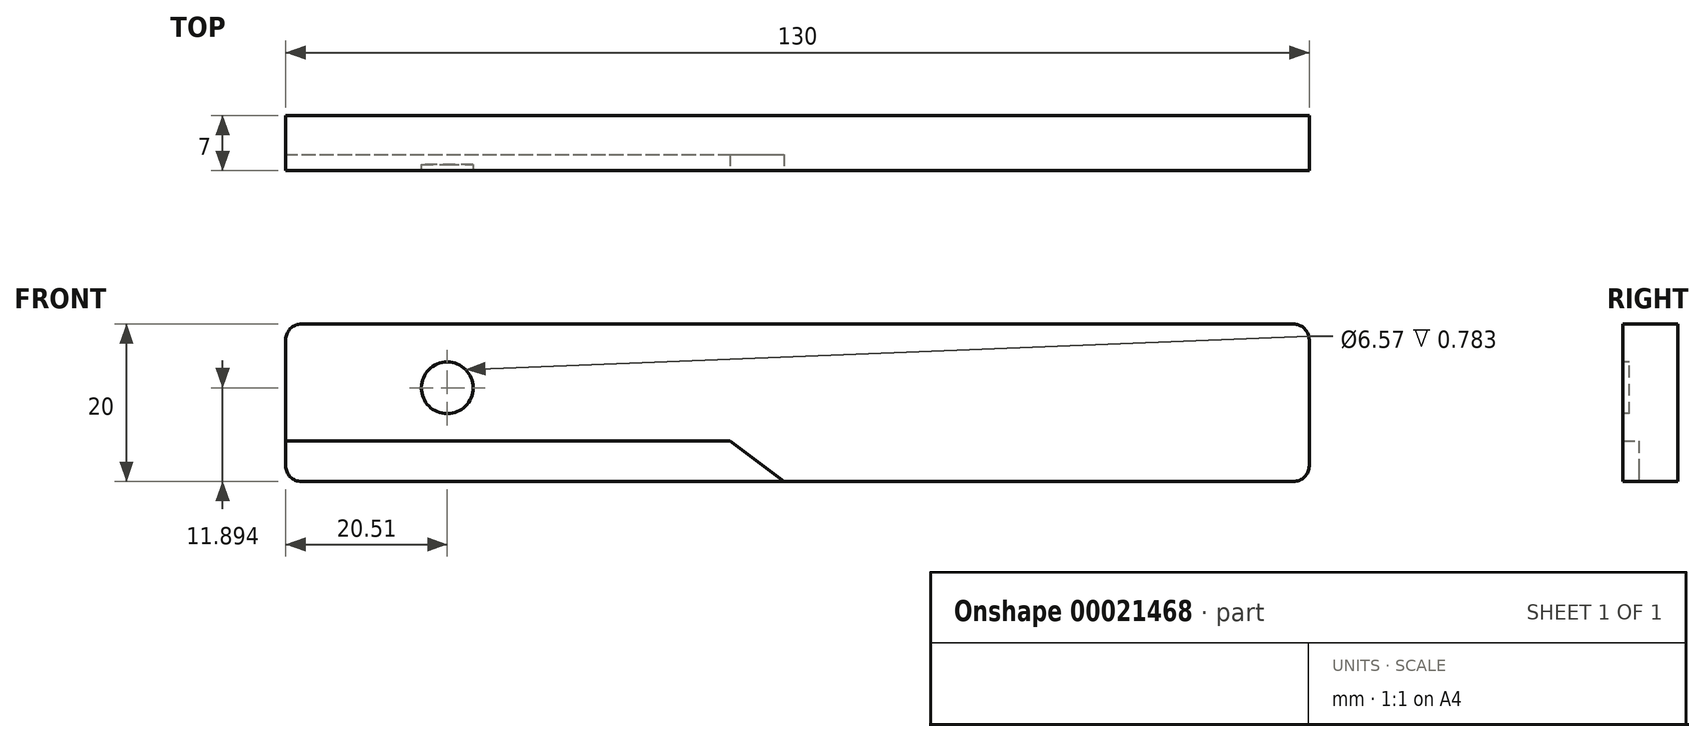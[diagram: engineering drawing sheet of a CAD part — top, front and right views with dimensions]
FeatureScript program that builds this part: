
annotation { "Feature Type Name" : "Feature", "Feature Type Description" : "" }
export const myFeature = defineFeature(function(context is Context, id is Id, definition is map)
    precondition{}
    {
        {
            var Q0;
            Q0=qCreatedBy(makeId("Front.planeOp"),FACE);
            var sketch = newSketch(context, id + "F0", { "sketchPlane" : qUnion([Q0])});
            skLineSegment(sketch, "E0.rect.bottom", {"start": v(63, -10) * mm, "end": v(-63, -10) * mm});
            skLineSegment(sketch, "E0.rect.top", {"start": v(63, 10) * mm, "end": v(-63, 10) * mm});
            skLineSegment(sketch, "E0.rect.left", {"start": v(65, -8) * mm, "end": v(65, 8) * mm});
            skLineSegment(sketch, "E0.rect.right", {"start": v(-65, -8) * mm, "end": v(-65, 8) * mm});
            skPoint(sketch, "E0.rect.middle", {"position": v(0, 0) * mm});
            skPoint(sketch, "E1.visualSharp", {"position": v(-65, 10) * mm});
            skArc(sketch, "E1.filletArc", {"start": v(-63, 10) * mm, "mid": v(-64.41, 9.41) * mm, "end": v(-65, 8) * mm});
            skPoint(sketch, "E2.visualSharp", {"position": v(65, 10) * mm});
            skArc(sketch, "E2.filletArc", {"start": v(65, 8) * mm, "mid": v(64.41, 9.41) * mm, "end": v(63, 10) * mm});
            skPoint(sketch, "E3.visualSharp", {"position": v(65, -10) * mm});
            skArc(sketch, "E3.filletArc", {"start": v(63, -10) * mm, "mid": v(64.41, -9.41) * mm, "end": v(65, -8) * mm});
            skPoint(sketch, "E4.visualSharp", {"position": v(-65, -10) * mm});
            skArc(sketch, "E4.filletArc", {"start": v(-65, -8) * mm, "mid": v(-64.41, -9.41) * mm, "end": v(-63, -10) * mm});
            skSolve(sketch);
        }
        {
            var Q0;
            Q0 = qSketchRegion(id + "F0", true);
            extrude(context, id + "F1", {"entities" : qUnion([Q0]), "oppositeDirection" : true, "depth" : 7 * mm});
        }
        {
            var Q0;
            Q0=makeQuery(id+"F1.opExtrude","CAP_FACE",FACE,{"disambiguationData":[OSD([sQuery(id+"F0.wireOp",EDGE,"E0.rect.bottom"),sQuery(id+"F0.wireOp",EDGE,"E0.rect.top"),sQuery(id+"F0.wireOp",EDGE,"E0.rect.left"),sQuery(id+"F0.wireOp",EDGE,"E0.rect.right"),sQuery(id+"F0.wireOp",EDGE,"E1.filletArc"),sQuery(id+"F0.wireOp",EDGE,"E2.filletArc"),sQuery(id+"F0.wireOp",EDGE,"E3.filletArc"),sQuery(id+"F0.wireOp",EDGE,"E4.filletArc")])],"isStart":true});
            var sketch = newSketch(context, id + "F2", { "sketchPlane" : qUnion([Q0])});
            skLineSegment(sketch, "E5", {"start": v(-69.01, -4.87) * mm, "end": v(-8.6, -4.87) * mm});
            skLineSegment(sketch, "E6", {"start": v(-8.6, -4.87) * mm, "end": v(10.6, -19.19) * mm});
            skLineSegment(sketch, "E7", {"start": v(10.6, -19.19) * mm, "end": v(-70.73, -19.19) * mm});
            skLineSegment(sketch, "E8", {"start": v(-70.73, -19.19) * mm, "end": v(-69.01, -4.87) * mm});
            skSolve(sketch);
        }
        {
            var Q0;
            Q0 = qSketchRegion(id + "F2", true);
            extrude(context, id + "F3", {"entities" : qUnion([Q0]), "operationType" : NewBodyOperationType.REMOVE, "oppositeDirection" : true, "depth" : 2.05 * mm});
        }
        {
            var Q0;
            Q0=makeQuery(id+"F1.opExtrude","CAP_FACE",FACE,{"disambiguationData":[OSD([sQuery(id+"F0.wireOp",EDGE,"E0.rect.bottom"),sQuery(id+"F0.wireOp",EDGE,"E0.rect.top"),sQuery(id+"F0.wireOp",EDGE,"E0.rect.left"),sQuery(id+"F0.wireOp",EDGE,"E0.rect.right"),sQuery(id+"F0.wireOp",EDGE,"E1.filletArc"),sQuery(id+"F0.wireOp",EDGE,"E2.filletArc"),sQuery(id+"F0.wireOp",EDGE,"E3.filletArc"),sQuery(id+"F0.wireOp",EDGE,"E4.filletArc")])],"isStart":true});
            var sketch = newSketch(context, id + "F4", { "sketchPlane" : qUnion([Q0])});
            skCircle(sketch, "E9", {"center": v(-44.5, 1.9) * mm, "radius": 3.29 * mm});
            skSolve(sketch);
        }
        {
            var Q0;
            Q0 = qSketchRegion(id + "F4", true);
            extrude(context, id + "F5", {"entities" : qUnion([Q0]), "operationType" : NewBodyOperationType.REMOVE, "oppositeDirection" : true, "depth" : 0.78 * mm});
        }
    });
